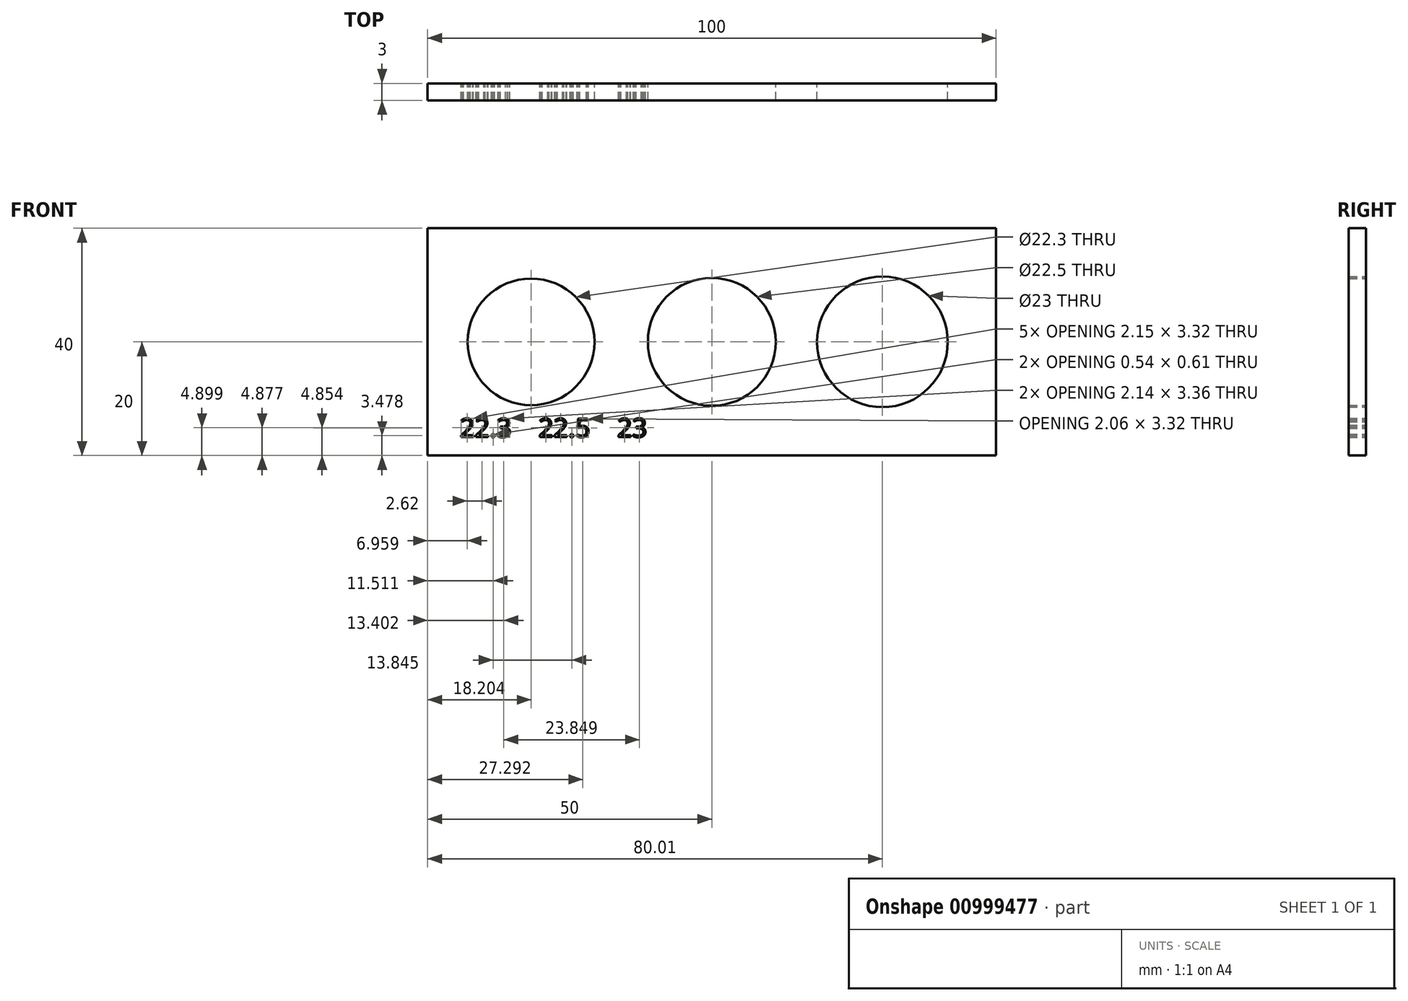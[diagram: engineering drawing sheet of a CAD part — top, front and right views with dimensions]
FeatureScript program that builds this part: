
annotation { "Feature Type Name" : "Feature", "Feature Type Description" : "" }
export const myFeature = defineFeature(function(context is Context, id is Id, definition is map)
    precondition{}
    {
        {
            var Q0;
            Q0=qCreatedBy(makeId("Front.planeOp"),FACE);
            var sketch = newSketch(context, id + "F0", { "sketchPlane" : qUnion([Q0])});
            skLineSegment(sketch, "E0.bottom", {"start": v(-50, 20) * mm, "end": v(50, 20) * mm});
            skLineSegment(sketch, "E0.top", {"start": v(-50, -20) * mm, "end": v(50, -20) * mm});
            skLineSegment(sketch, "E0.left", {"start": v(-50, 20) * mm, "end": v(-50, -20) * mm});
            skLineSegment(sketch, "E0.right", {"start": v(50, 20) * mm, "end": v(50, -20) * mm});
            skPoint(sketch, "E0.middle", {"position": v(0, 0) * mm});
            skCircle(sketch, "E1", {"center": v(-31.8, 0) * mm, "radius": 11.15 * mm});
            skCircle(sketch, "E2", {"center": v(0, 0) * mm, "radius": 11.25 * mm});
            skCircle(sketch, "E3", {"center": v(30, 0) * mm, "radius": 11.5 * mm});
            skText(sketch, "E4", { "text": "22.3    22.5    23", "fontName": "OpenSans-Regular.ttf"});
            const initialGuessF0  = {"E4": [-0.04434, -0.01676, 1, 0, 0.0033]};
            skSetInitialGuess(sketch, initialGuessF0);
            skSolve(sketch);
        }
        {
            var Q0;
            Q0=makeQuery(id+"F0.imprint","IMPRINT",FACE,{"disambiguationData":[TD([[makeQuery(id+"F0.imprint","IMPRINT",EDGE,{"derivedFrom":sQuery(id+"F0.wireOp",EDGE,"E0.bottom")}),-1.0]])]});
            extrude(context, id + "F1", {"entities" : qUnion([Q0]), "depth" : 3 * mm, "offsetDistance" : 25 * mm});
        }
    });
